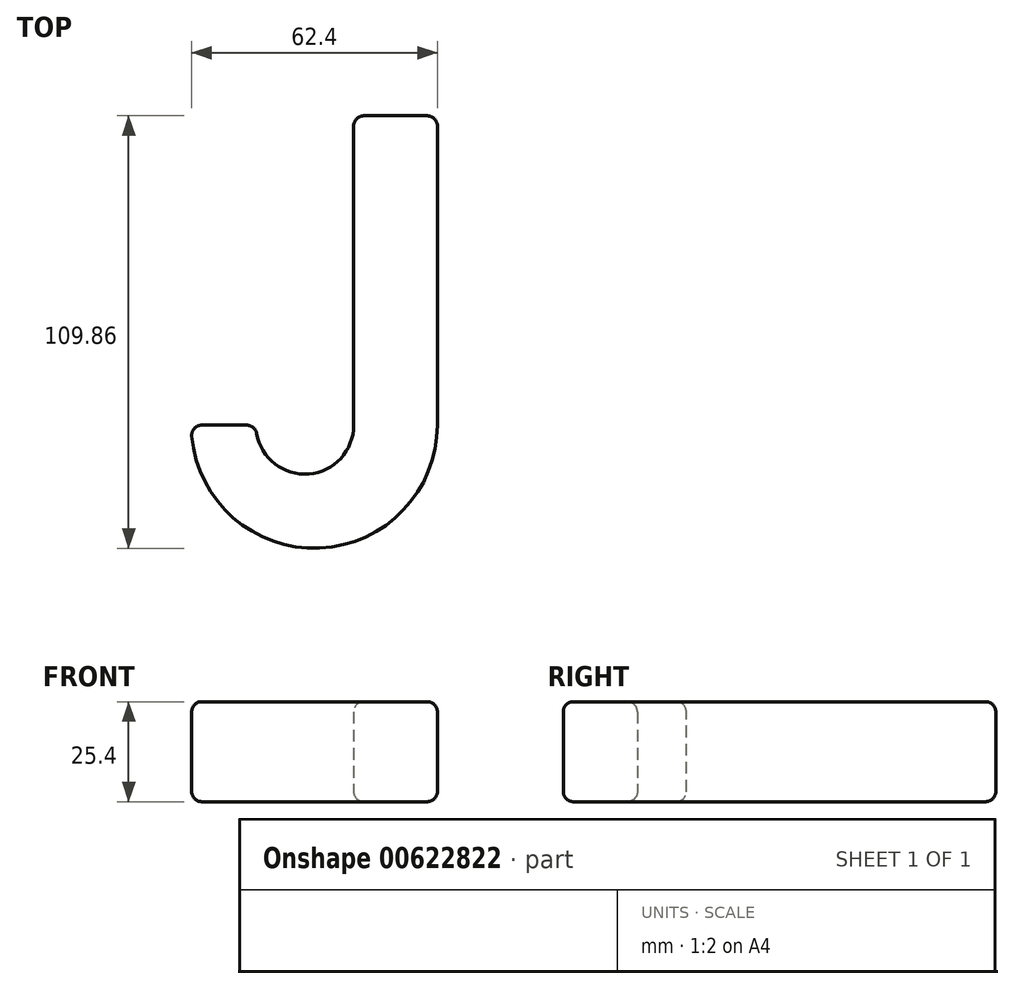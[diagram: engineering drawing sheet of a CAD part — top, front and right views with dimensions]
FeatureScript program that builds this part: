
annotation { "Feature Type Name" : "Feature", "Feature Type Description" : "" }
export const myFeature = defineFeature(function(context is Context, id is Id, definition is map)
    precondition{}
    {
        {
            var Q0;
            Q0=qCreatedBy(makeId("Top.planeOp"),FACE);
            var sketch = newSketch(context, id + "F0", { "sketchPlane" : qUnion([Q0])});
            skLineSegment(sketch, "E0", {"start": v(-100.25, 78.6) * mm, "end": v(-79.01, 78.6) * mm});
            skLineSegment(sketch, "E1", {"start": v(-100.25, 78.6) * mm, "end": v(-100.25, 0) * mm});
            skLineSegment(sketch, "E2", {"start": v(-79.01, 78.6) * mm, "end": v(-79.01, 0) * mm});
            skArc(sketch, "E3", {"start": v(-141.53, 0) * mm, "mid": v(-110.27, -31.26) * mm, "end": v(-79.01, 0) * mm});
            skArc(sketch, "E4", {"start": v(-125.11, 0) * mm, "mid": v(-112.68, -12.43) * mm, "end": v(-100.25, 0) * mm});
            skLineSegment(sketch, "E5", {"start": v(-125.11, 0) * mm, "end": v(-141.53, 0) * mm});
            skSolve(sketch);
        }
        {
            var Q0;
            Q0=qSketchRegion(id+"F0",true);
            extrude(context, id + "F1", {"entities" : qUnion([Q0]), "depth" : 25.4 * mm, "offsetDistance" : 25.4 * mm});
        }
        {
            var Q0;
            Q0=makeQuery(id+"F1.opExtrude","CAP_FACE",FACE,{"disambiguationData":[OSD([sQuery(id+"F0.wireOp",EDGE,"E0"),sQuery(id+"F0.wireOp",EDGE,"E1"),sQuery(id+"F0.wireOp",EDGE,"E2"),sQuery(id+"F0.wireOp",EDGE,"E3"),sQuery(id+"F0.wireOp",EDGE,"E4"),sQuery(id+"F0.wireOp",EDGE,"E5")])],"isStart":false});
            var Q1;
            Q1=makeQuery(id+"F1.opExtrude","CAP_FACE",FACE,{"disambiguationData":[OSD([sQuery(id+"F0.wireOp",EDGE,"E0"),sQuery(id+"F0.wireOp",EDGE,"E1"),sQuery(id+"F0.wireOp",EDGE,"E2"),sQuery(id+"F0.wireOp",EDGE,"E3"),sQuery(id+"F0.wireOp",EDGE,"E4"),sQuery(id+"F0.wireOp",EDGE,"E5")])],"isStart":true});
            var Q2;
            Q2=makeQuery(id+"F1.opExtrude","SWEPT_FACE",FACE,{"disambiguationData":[OSD([sQuery(id+"F0.wireOp",EDGE,"E0")])]});
            var Q3;
            Q3=makeQuery(id+"F1.opExtrude","SWEPT_FACE",FACE,{"disambiguationData":[OSD([sQuery(id+"F0.wireOp",EDGE,"E5")])]});
            fillet(context, id + "F2", {"entities" : qUnion([Q0, Q1, Q2, Q3]), "radius" : 2.54 * mm, "tangentPropagation" : true, "allowEdgeOverflow" : false});
        }
    });
